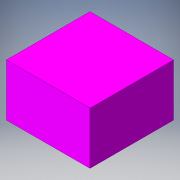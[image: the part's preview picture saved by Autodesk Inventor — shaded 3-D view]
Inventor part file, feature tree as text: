
AUTODESK INVENTOR PART (.ipt)
format: ipt  version: 2016 (Build 200138000, 138)  size: 90,112 bytes
history: native  units: in
note: dims shown in document units (in); Inventor stores cm internally (conversion verified against a paired STEP export)
features: extrude x1, sketch x1
ambient origin geometry x8: Origin, YZ Plane, XZ Plane, XY Plane, X Axis, Y Axis, Z Axis, Center Point
bodies: Solid1 (feature_tree)
feature tree (2):
  extrude  "Extrusion1"  Depth=1.25in
  sketch  "Sketch1"  dims[d0=2.0in d1=1.25in d2=2.0in d3=0.0in]
